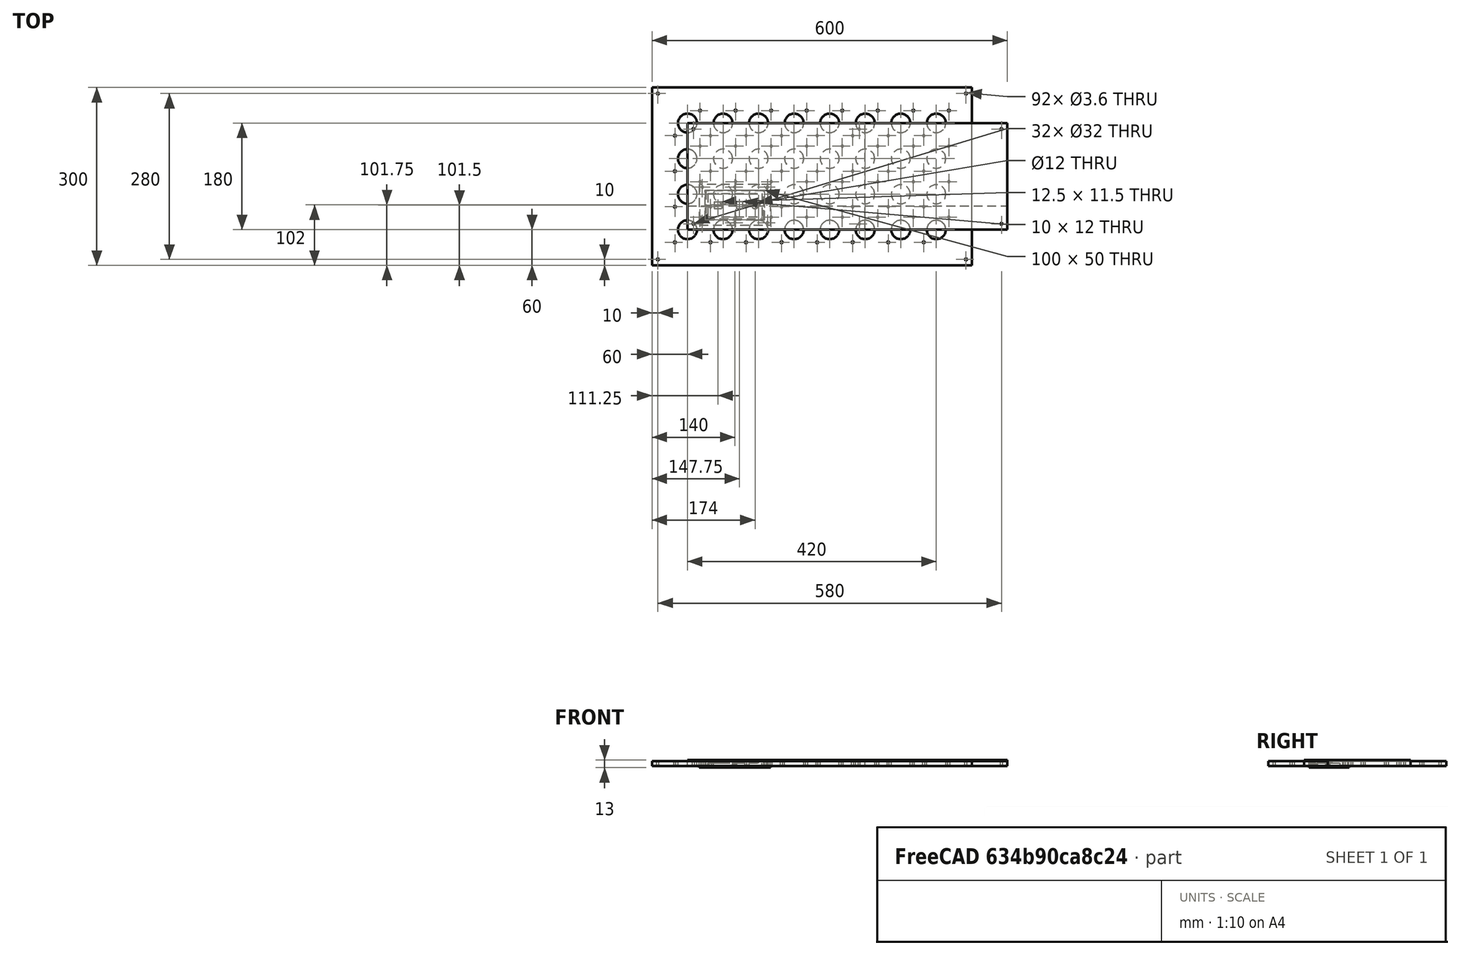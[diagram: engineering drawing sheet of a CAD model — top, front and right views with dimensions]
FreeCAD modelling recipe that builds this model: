
FCSTD DOCUMENT  (FreeCAD 0.14R3702 (Git))
Label: mesa
License: CC-BY 3.0
LicenseURL: http://creativecommons.org/licenses/by/3.0/
objects: Part::Cylinder×10, Part::Box×10, Part::Cut×10, Part::FeaturePython×7, Part::MultiFuse×5, Part::Feature×2, Part::Extrusion×2
note: 46 computed .brp shape members not serialized (recipe doc carries the construction recipe); baked Part::Feature solids carry a one-line shape summary decoded from their .brp

FEATURE [Part::Cylinder] Cylinder
  Angle = 360
  Height = 10
  Radius = 16
FEATURE [Part::Cylinder] Cylinder001
  Angle = 360
  Height = 10
  Placement = pos=(-30,0,0) rot=(0,0,1;0rad)
  Radius = 1.8
FEATURE [Part::Cylinder] Cylinder002
  Angle = 360
  Height = 10
  Placement = pos=(30,0,0) rot=(0,0,1;0rad)
  Radius = 1.8
FEATURE [Part::MultiFuse] Fusion  label="tornillos"
  Shapes = -> [Cylinder001,Cylinder002]
FEATURE [Part::MultiFuse] Fusion001  label="agujero"
  Placement = pos=(0,0,0) rot=(0,0,1;0.785398rad)
  Shapes = -> [Fusion,Cylinder]
FEATURE [Part::FeaturePython] Array  # Draft array (typed FeaturePython)
  Angle = 360
  ArrayType = 0
  Axis = (0,0,1)
  Base = -> Fusion001
  Center = (0,0,0)
  IntervalX = (60,0,0)
  IntervalY = (0,60,0)
  IntervalZ = (0,0,1)
  NumberPolar = 1
  NumberX = 8
  NumberY = 4
  NumberZ = 1
FEATURE [Part::Box] Box  label="Cube"
  Height = 8
  Length = 540
  Placement = pos=(-60,-60,0) rot=(0,0,1;0rad)
  Width = 300
FEATURE [Part::Cut] Cut  label="002"
  Base = -> Box
  Tool = -> Array
FEATURE [Part::Box] Box001  label="lado-largo"
  Height = 8
  Length = 540
  Width = 40
FEATURE [Part::Box] Box003  label="lado-corto"
  Height = 8
  Length = 300
  Width = 40
FEATURE [Part::Box] Box004  label="001"
  Height = 8
  Length = 300
  Width = 180
FEATURE [Part::Box] Box005
  Height = 8
  Length = 300
  Width = 180
FEATURE [Part::Box] Box006  label="agujero-jacks"
  Height = 8
  Length = 100
  Placement = pos=(30,17,0) rot=(0,0,1;0rad)
  Width = 50
FEATURE [Part::Cut] Cut001  label="cara-corta-agujero"
  Base = -> Box005
  Tool = -> Box006
FEATURE [Part::Cylinder] Cylinder003
  Angle = 360
  Height = 10
  Placement = pos=(25,12,0) rot=(0,0,1;0rad)
  Radius = 1.8
FEATURE [Part::FeaturePython] Array001  label="tornillos001"  # Draft array (typed FeaturePython)
  Angle = 360
  ArrayType = 0
  Axis = (0,0,1)
  Base = -> Cylinder003
  Center = (0,0,0)
  IntervalX = (55,0,0)
  IntervalY = (0,60,0)
  IntervalZ = (0,0,1)
  NumberPolar = 1
  NumberX = 3
  NumberY = 2
  NumberZ = 1
FEATURE [Part::Cut] Cut002
  Base = -> Cut001
  Tool = -> Array001
FEATURE [Part::Cylinder] Cylinder004
  Angle = 360
  Height = 10
  Placement = pos=(10,10,0) rot=(0,0,1;0rad)
  Radius = 1.8
FEATURE [Part::FeaturePython] Array002  # Draft array (typed FeaturePython)
  Angle = 360
  ArrayType = 0
  Axis = (0,0,1)
  Base = -> Cylinder004
  Center = (0,0,0)
  IntervalX = (280,0,0)
  IntervalY = (0,160,0)
  IntervalZ = (0,0,1)
  NumberPolar = 1
  NumberX = 2
  NumberY = 2
  NumberZ = 1
FEATURE [Part::Cut] Cut003  label="cara-corta-conectores"
  Base = -> Cut002
  Tool = -> Array002
FEATURE [Part::Cylinder] Cylinder005
  Angle = 360
  Height = 10
  Placement = pos=(10,10,0) rot=(0,0,1;0rad)
  Radius = 1.8
FEATURE [Part::FeaturePython] Array003  # Draft array (typed FeaturePython)
  Angle = 360
  ArrayType = 0
  Axis = (0,0,1)
  Base = -> Cylinder005
  Center = (0,0,0)
  IntervalX = (280,0,0)
  IntervalY = (0,160,0)
  IntervalZ = (0,0,1)
  NumberPolar = 1
  NumberX = 2
  NumberY = 2
  NumberZ = 1
FEATURE [Part::Cut] Cut004  label="cara-corta"
  Base = -> Box004
  Tool = -> Array003
FEATURE [Part::Cylinder] Cylinder008
  Angle = 360
  Height = 10
  Placement = pos=(-50,-50,0) rot=(0,0,1;0rad)
  Radius = 1.8
FEATURE [Part::FeaturePython] Array006  # Draft array (typed FeaturePython)
  Angle = 360
  ArrayType = 0
  Axis = (0,0,1)
  Base = -> Cylinder008
  Center = (0,0,0)
  IntervalX = (520,0,0)
  IntervalY = (0,280,0)
  IntervalZ = (0,0,1)
  NumberPolar = 1
  NumberX = 2
  NumberY = 2
  NumberZ = 1
FEATURE [Part::Cut] Cut007  label="base"
  Base = -> Cut
  Tool = -> Array006
FEATURE [Part::Box] Box007  label="Cube001"
  Height = 10
  Length = 540
  Width = 180
FEATURE [Part::Cylinder] Cylinder009
  Angle = 360
  Height = 10
  Placement = pos=(10,10,0) rot=(0,0,1;0rad)
  Radius = 1.8
FEATURE [Part::FeaturePython] Array007  # Draft array (typed FeaturePython)
  Angle = 360
  ArrayType = 0
  Axis = (0,0,1)
  Base = -> Cylinder009
  Center = (0,0,0)
  IntervalX = (520,0,0)
  IntervalY = (0,160,0)
  IntervalZ = (0,0,1)
  NumberPolar = 1
  NumberX = 2
  NumberY = 2
  NumberZ = 1
FEATURE [Part::Cut] Cut008  label="cara-larga"
  Base = -> Box007
  Tool = -> Array007
FEATURE [Part::Feature] Face
  shape: bbox 120.3 x 68.24 x 2e-07 mm, 1 faces, 0 solids (baked)
FEATURE [Part::Feature] Face001
  shape: bbox 97.69 x 47.35 x 2e-07 mm, 1 faces, 0 solids (baked)
FEATURE [Part::Extrusion] Extrude001  label="pequeño"
  Base = -> Face001
  Dir = (0,0,8)
  Solid = false
FEATURE [Part::Extrusion] Extrude002  label="grande"
  Base = -> Face
  Dir = (0,0,-3)
  Solid = false
FEATURE [Part::MultiFuse] Fusion002  label="base001"
  Shapes = -> [Extrude002,Extrude001]
FEATURE [Part::Box] Box008  label="USB"
  Height = 18
  Length = 12.5
  Width = 11.5
FEATURE [Part::Box] Box009  label="JACK"
  Height = 18
  Length = 10
  Placement = pos=(37.75,0,0) rot=(0,0,1;0rad)
  Width = 12
FEATURE [Part::MultiFuse] Fusion003
  Placement = pos=(45,36,-6) rot=(0,0,1;0rad)
  Shapes = -> [Box008,Box009]
FEATURE [Part::Cylinder] Cylinder010
  Angle = 360
  Height = 18
  Placement = pos=(114,41.5,-6) rot=(0,0,1;0rad)
  Radius = 6
FEATURE [Part::MultiFuse] Fusion004  label="conectores"
  Shapes = -> [Fusion003,Cylinder010]
FEATURE [Part::Cut] Cut009
  Base = -> Fusion002
  Tool = -> Fusion004
FEATURE [Part::Cylinder] Cylinder011
  Angle = 360
  Height = 10
  Placement = pos=(25,12,0) rot=(0,0,1;0rad)
  Radius = 1.8
FEATURE [Part::FeaturePython] Array008  label="tornillos002"  # Draft array (typed FeaturePython)
  Angle = 360
  ArrayType = 0
  Axis = (0,0,1)
  Base = -> Cylinder011
  Center = (0,0,0)
  IntervalX = (55,0,0)
  IntervalY = (0,60,0)
  IntervalZ = (0,0,1)
  NumberPolar = 1
  NumberX = 3
  NumberY = 2
  NumberZ = 1
  Placement = pos=(0,0,-3) rot=(0,0,1;0rad)
FEATURE [Part::Cut] Cut010
  Base = -> Cut009
  Tool = -> Array008
FEATURE [Part::Box] Box010  label="hueco grande componentes"
  Height = 21
  Length = 92
  Placement = pos=(34,22,-16) rot=(0,0,1;0rad)
  Width = 39
FEATURE [Part::Cut] Cut011  label="tapa-conectores"
  Base = -> Cut010
  Tool = -> Box010
